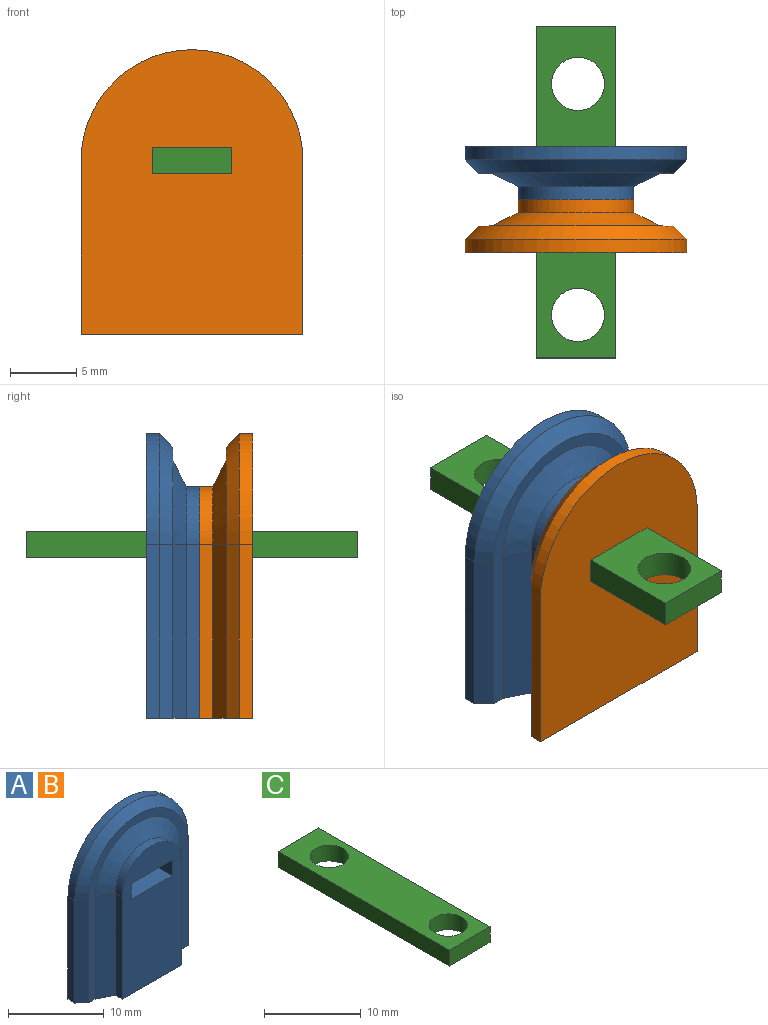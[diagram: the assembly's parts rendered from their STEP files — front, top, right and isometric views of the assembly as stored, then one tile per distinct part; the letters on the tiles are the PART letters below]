
ASSEMBLY  parts=3 mates=2
PART A: 20 faces, bbox 16.7x4x21.4 mm
  f0: plane 20.43x14.71mm, normal (0,-1,0), area 47.7mm2, adj f5,f14,f15,f16,f17,f18,f19
  f1: plane 6x4mm, normal (0,0,-1), area 24mm2, adj f2,f8,f9,f13
  f2: plane 4x2mm, normal (-1,0,0), area 8mm2, adj f1,f3,f9,f13
  f3: plane 6x4mm, normal (0,0,1), area 24mm2, adj f2,f8,f9,f13
  f4: plane 13.07x1mm, normal (-1,0,0), area 13.1mm2, adj f5,f7,f9,f17
  f5: plane 16.71x4mm, normal (0,0,-1), area 51.8mm2, adj f0,f4,f6,f9,f10,f12,f13,f14
  f6: plane 13.07x1mm, normal (1,0,0), area 13.1mm2, adj f5,f7,f9,f19
  f7: cylinder r=8.36mm len=16.71mm, axis (0,1,0), area 26.2mm2, adj f4,f6,f9,f18
  f8: plane 4x2mm, normal (1,0,0), area 8mm2, adj f1,f3,f9,f13
  f9: plane 21.43x16.71mm, normal (0,1,0), area 316.1mm2, adj f1,f2,f3,f4,f5,f6,f7,f8
  f10: plane 13.07x1mm, normal (1,0,0), area 13.1mm2, adj f5,f11,f13,f16
  f11: cylinder r=4.36mm len=8.71mm, axis (0,-1,0), area 13.7mm2, adj f10,f12,f13,f15
  f12: plane 13.07x1mm, normal (-1,0,0), area 13.1mm2, adj f5,f11,f13,f14
  f13: plane 17.43x8.71mm, normal (0,-1,0), area 131.7mm2, adj f1,f2,f3,f5,f8,f10,f11,f12
  f14: plane 13.07x2mm, normal (-0.45,-0.89,0), area 29.2mm2, adj f0,f5,f12,f15
  f15: cone r=4.36mm half-angle=63.4deg, axis (0,1,0), area 37.6mm2, adj f0,f11,f14,f16
  f16: plane 13.07x2mm, normal (0.45,-0.89,0), area 29.2mm2, adj f0,f5,f10,f15
  f17: plane 13.07x1mm, normal (-0.71,-0.71,0), area 18.5mm2, adj f0,f4,f5,f18
  f18: cone r=7.36mm half-angle=45deg, axis (0,1,0), area 34.9mm2, adj f0,f7,f17,f19
  f19: plane 13.07x1mm, normal (0.71,-0.71,0), area 18.5mm2, adj f0,f5,f6,f18
PART B: same geometry as A
PART C: 8 faces, bbox 6x25x2 mm
  f0: plane 25x5.99mm, normal (0,0,-1), area 124.6mm2, adj f2,f3,f4,f5,f6,f7
  f1: plane 25x5.99mm, normal (0,0,1), area 124.6mm2, adj f2,f3,f4,f5,f6,f7
  f2: plane 25x1.99mm, normal (-1,0,0), area 49.7mm2, adj f0,f1,f4,f5
  f3: plane 25x1.99mm, normal (1,0,0), area 49.7mm2, adj f0,f1,f4,f5
  f4: plane 5.99x1.99mm, normal (0,-1,0), area 11.9mm2, adj f0,f1,f2,f3
  f5: plane 5.99x1.99mm, normal (0,1,0), area 11.9mm2, adj f0,f1,f2,f3
  f6: cylinder r=2mm len=4mm, axis (0,0,-1), area 25mm2, adj f0,f1
  f7: cylinder r=2mm len=4mm, axis (0,0,-1), area 25mm2, adj f0,f1
PLACE A rot(axis=(0,1,0),0deg) t=(-16.42,-4.07,-24.48)mm
PLACE B rot(axis=(0,0,1),180deg) t=(-59.43,-12.07,-24.48)mm
PLACE C t=(5.94,4.99,-12.4)mm
MATE fastened A.f13 <-> B.f13  axis (0,-1,0) through (-37.93,-8.07,-16.64)mm
MATE slider A.f7 <-> C.f4  axis (0,-1,0) through (-37.93,-8.07,-11.41)mm
